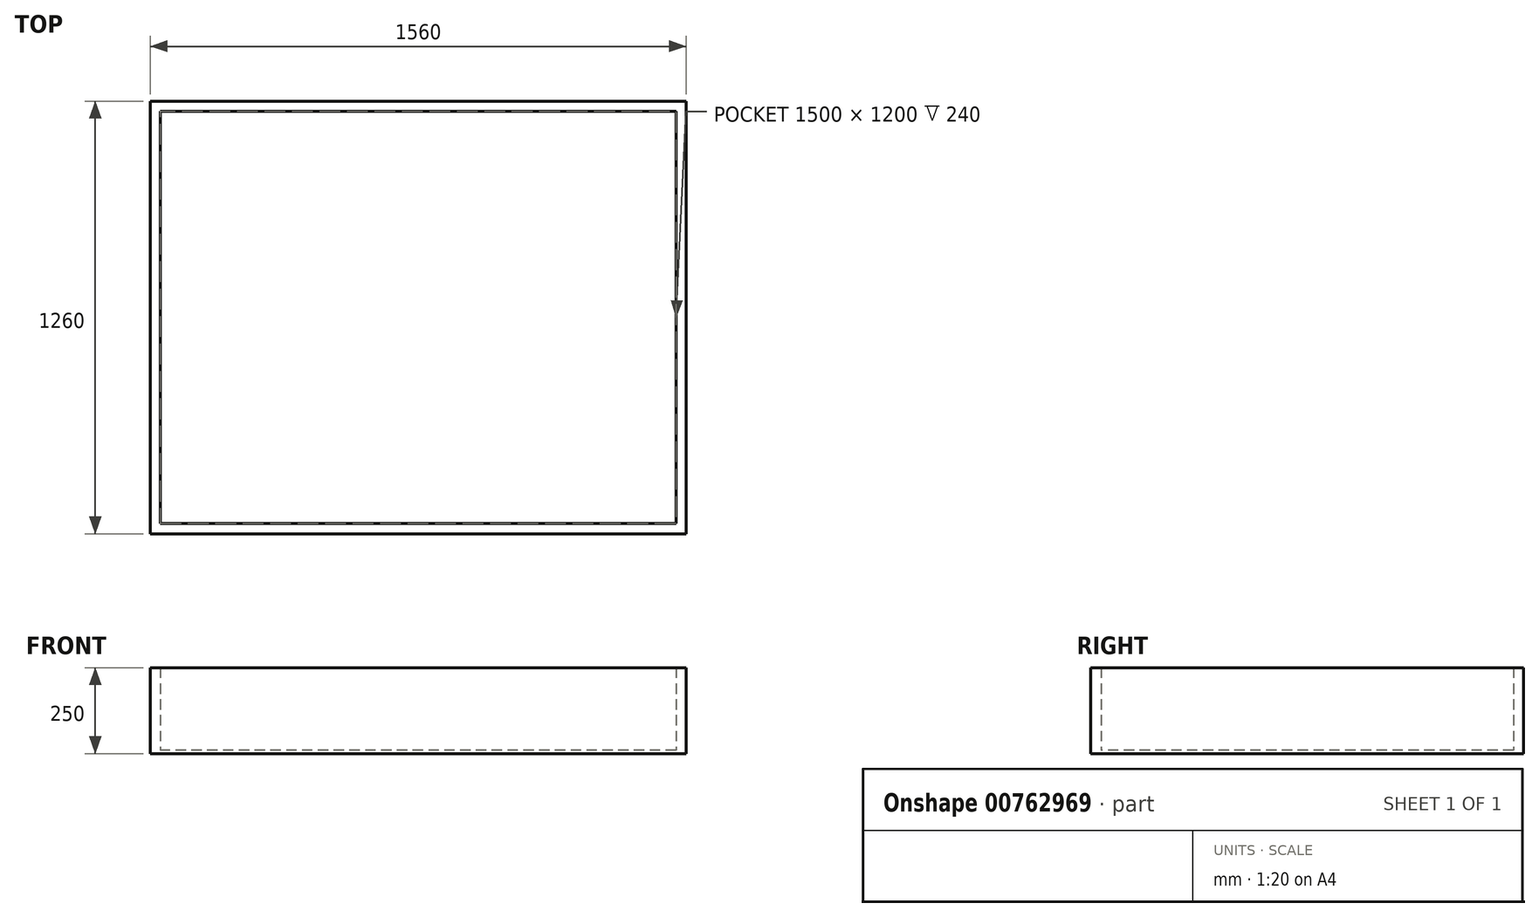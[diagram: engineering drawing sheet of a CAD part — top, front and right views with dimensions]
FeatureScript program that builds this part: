
annotation { "Feature Type Name" : "Feature", "Feature Type Description" : "" }
export const myFeature = defineFeature(function(context is Context, id is Id, definition is map)
    precondition{}
    {
        {
            var Q0;
            Q0=qCreatedBy(makeId("Top.planeOp"),FACE);
            var sketch = newSketch(context, id + "F0", { "sketchPlane" : qUnion([Q0])});
            skLineSegment(sketch, "E0.bottom", {"start": v(750, 600) * mm, "end": v(-750, 600) * mm});
            skLineSegment(sketch, "E0.top", {"start": v(750, -600) * mm, "end": v(-750, -600) * mm});
            skLineSegment(sketch, "E0.left", {"start": v(750, 600) * mm, "end": v(750, -600) * mm});
            skLineSegment(sketch, "E0.right", {"start": v(-750, 600) * mm, "end": v(-750, -600) * mm});
            skPoint(sketch, "E0.middle", {"position": v(0, 0) * mm});
            skLineSegment(sketch, "E1.0", {"start": v(780, 630) * mm, "end": v(-780, 630) * mm});
            skLineSegment(sketch, "E1.1", {"start": v(780, 630) * mm, "end": v(780, -630) * mm});
            skLineSegment(sketch, "E1.2", {"start": v(780, -630) * mm, "end": v(-780, -630) * mm});
            skLineSegment(sketch, "E1.3", {"start": v(-780, 630) * mm, "end": v(-780, -630) * mm});
            skSolve(sketch);
        }
        {
            var Q0;
            Q0 = qSketchRegion(id + "F0", true);
            extrude(context, id + "F1", {"entities" : qUnion([Q0]), "depth" : 250 * mm, "offsetDistance" : 25 * mm});
        }
        {
            var Q0;
            Q0=makeQuery(id+"F0.imprint","IMPRINT",FACE,{"disambiguationData":[TD([[makeQuery(id+"F0.imprint","IMPRINT",EDGE,{"derivedFrom":sQuery(id+"F0.wireOp",EDGE,"E0.bottom")}),-1.0]])]});
            var Q1;
            Q1=makeQuery(id+"F0.imprint","IMPRINT",FACE,{"disambiguationData":[TD([[makeQuery(id+"F0.imprint","IMPRINT",EDGE,{"derivedFrom":sQuery(id+"F0.wireOp",EDGE,"E0.bottom")}),1.0]])]});
            extrude(context, id + "F2", {"entities" : qUnion([Q0, Q1]), "operationType" : NewBodyOperationType.ADD, "depth" : 10 * mm, "offsetDistance" : 25 * mm});
        }
    });
